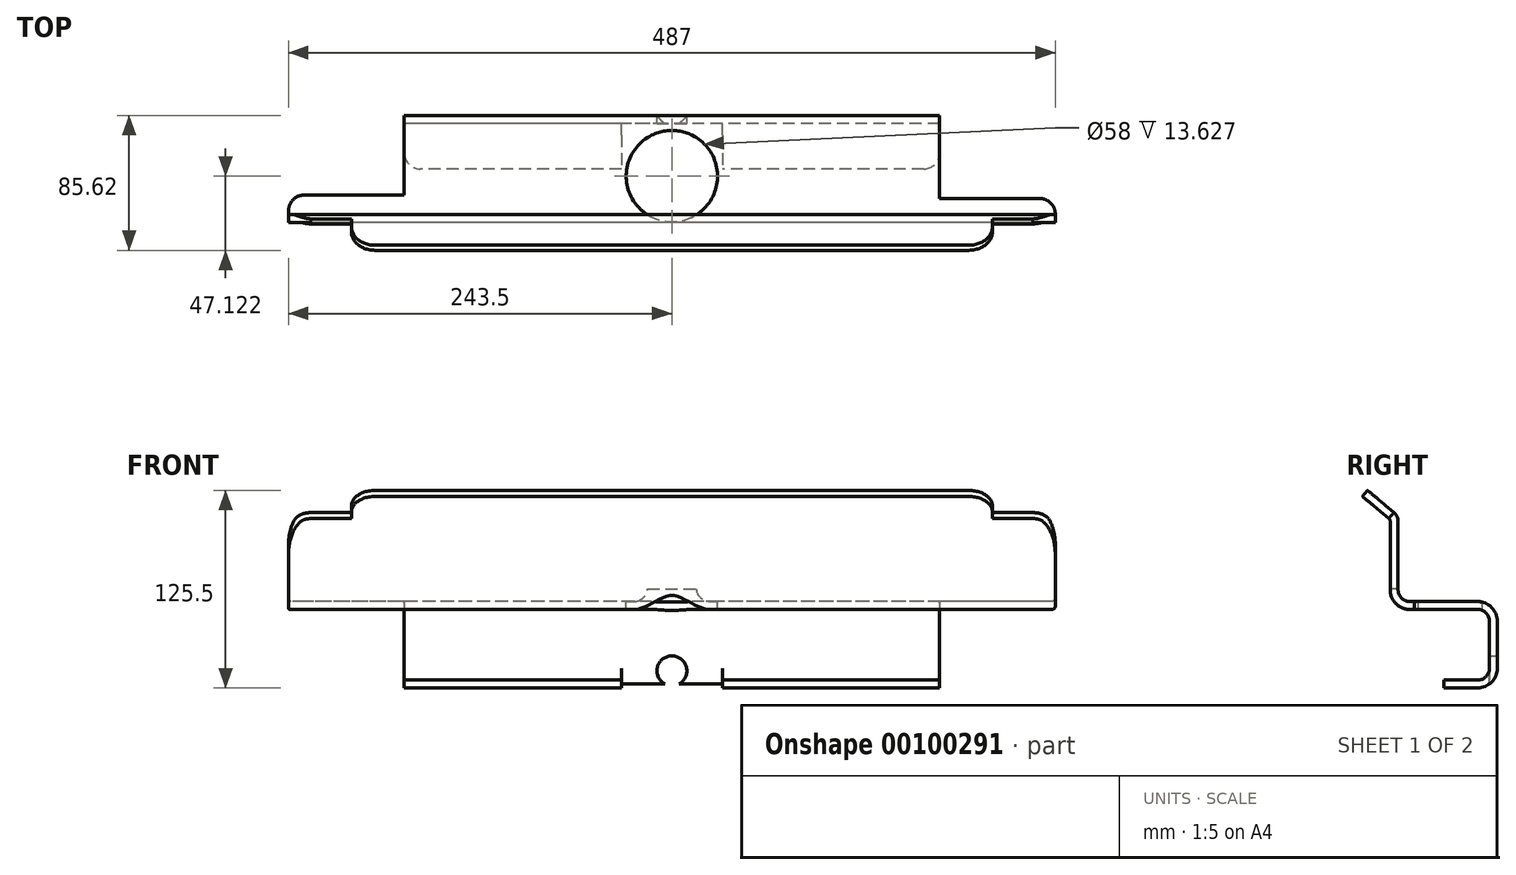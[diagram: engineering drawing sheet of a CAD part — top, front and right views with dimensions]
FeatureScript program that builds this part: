
annotation { "Feature Type Name" : "Feature", "Feature Type Description" : "" }
export const myFeature = defineFeature(function(context is Context, id is Id, definition is map)
    precondition{}
    {
        {
            var Q0;
            Q0=qCreatedBy(makeId("Right.planeOp"),FACE);
            var sketch = newSketch(context, id + "F0", { "sketchPlane" : qUnion([Q0])});
            skArc(sketch, "E0", {"start": v(-37.83, 42.97) * mm, "mid": v(-38.06, 44.03) * mm, "end": v(-38.72, 44.89) * mm});
            skLineSegment(sketch, "E1", {"start": v(-55.45, 58.92) * mm, "end": v(-52.23, 62.75) * mm});
            skArc(sketch, "E2", {"start": v(-32.83, 42.97) * mm, "mid": v(-33.53, 46.14) * mm, "end": v(-35.5, 48.72) * mm});
            skArc(sketch, "E3", {"start": v(-32.83, -0.36) * mm, "mid": v(-30.63, -5.67) * mm, "end": v(-25.33, -7.86) * mm});
            skArc(sketch, "E4", {"start": v(30.17, -20.36) * mm, "mid": v(26.51, -11.52) * mm, "end": v(17.67, -7.86) * mm});
            skLineSegment(sketch, "E5", {"start": v(-3.79, -62.75) * mm, "end": v(-3.79, -57.75) * mm});
            skArc(sketch, "E6", {"start": v(17.67, -57.75) * mm, "mid": v(22.98, -55.55) * mm, "end": v(25.17, -50.25) * mm});
            skArc(sketch, "E7", {"start": v(25.17, -20.36) * mm, "mid": v(22.98, -15.06) * mm, "end": v(17.67, -12.86) * mm});
            skArc(sketch, "E8", {"start": v(-37.83, -0.36) * mm, "mid": v(-34.17, -9.2) * mm, "end": v(-25.33, -12.86) * mm});
            skArc(sketch, "E9", {"start": v(17.67, -62.75) * mm, "mid": v(26.51, -59.09) * mm, "end": v(30.17, -50.25) * mm});
            skLineSegment(sketch, "E10", {"start": v(-35.5, 48.72) * mm, "end": v(-52.23, 62.75) * mm});
            skLineSegment(sketch, "E11", {"start": v(-38.72, 44.89) * mm, "end": v(-55.45, 58.92) * mm});
            skLineSegment(sketch, "E12", {"start": v(-32.83, 42.97) * mm, "end": v(-32.83, -0.36) * mm});
            skLineSegment(sketch, "E13", {"start": v(-37.83, 42.97) * mm, "end": v(-37.83, -0.36) * mm});
            skLineSegment(sketch, "E14", {"start": v(-25.33, -7.86) * mm, "end": v(17.67, -7.86) * mm});
            skLineSegment(sketch, "E15", {"start": v(-25.33, -12.86) * mm, "end": v(17.67, -12.86) * mm});
            skLineSegment(sketch, "E16", {"start": v(30.17, -20.36) * mm, "end": v(30.17, -50.25) * mm});
            skLineSegment(sketch, "E17", {"start": v(25.17, -20.36) * mm, "end": v(25.17, -50.25) * mm});
            skLineSegment(sketch, "E18", {"start": v(17.67, -62.75) * mm, "end": v(-3.79, -62.75) * mm});
            skLineSegment(sketch, "E19", {"start": v(17.67, -57.75) * mm, "end": v(-3.79, -57.75) * mm});
            skLineSegment(sketch, "E20", {"start": v(0, 0) * mm, "end": v(-113.48, 0) * mm, "construction": true});
            skSolve(sketch);
        }
        {
            var Q0;
            Q0=qSketchRegion(id+"F0",true);
            extrude(context, id + "F1", {"entities" : qUnion([Q0]), "endBound" : BoundingType.SYMMETRIC, "depth" : 487 * mm});
        }
        {
            var Q0;
            Q0=qCreatedBy(makeId("Top.planeOp"),FACE);
            var sketch = newSketch(context, id + "F2", { "sketchPlane" : qUnion([Q0])});
            skLineSegment(sketch, "E21.0", {"start": v(243.5, 30.17) * mm, "end": v(-243.5, 30.17) * mm, "construction": true});
            skLineSegment(sketch, "E22.0", {"start": v(243.5, 25.17) * mm, "end": v(-243.5, 25.17) * mm, "construction": true});
            skLineSegment(sketch, "E23.0", {"start": v(243.5, -3.79) * mm, "end": v(-243.5, -3.79) * mm, "construction": true});
            skLineSegment(sketch, "E24.bottom", {"start": v(-346.92, 71.4) * mm, "end": v(-170, 71.4) * mm});
            skLineSegment(sketch, "E24.top", {"start": v(-346.92, -20.36) * mm, "end": v(-170, -20.36) * mm});
            skLineSegment(sketch, "E24.left", {"start": v(-346.92, 71.4) * mm, "end": v(-346.92, -20.36) * mm});
            skLineSegment(sketch, "E24.right", {"start": v(-170, 71.4) * mm, "end": v(-170, -20.36) * mm});
            skLineSegment(sketch, "E25.bottom", {"start": v(170, 71.4) * mm, "end": v(314.46, 71.4) * mm});
            skLineSegment(sketch, "E25.top", {"start": v(170, -22.45) * mm, "end": v(314.46, -22.45) * mm});
            skLineSegment(sketch, "E25.left", {"start": v(170, 71.4) * mm, "end": v(170, -22.45) * mm});
            skLineSegment(sketch, "E25.right", {"start": v(314.46, 71.4) * mm, "end": v(314.46, -22.45) * mm});
            skLineSegment(sketch, "E26", {"start": v(-346.92, 71.4) * mm, "end": v(192.66, 71.4) * mm, "construction": true});
            skSolve(sketch);
        }
        {
            var Q0;
            Q0=makeQuery(id+"F2.imprint","IMPRINT",FACE,{"disambiguationData":[TD([[makeQuery(id+"F2.imprint","IMPRINT",EDGE,{"derivedFrom":sQuery(id+"F2.wireOp",EDGE,"E24.bottom")}),-1.0]])]});
            var Q1;
            Q1=makeQuery(id+"F2.imprint","IMPRINT",FACE,{"disambiguationData":[TD([[makeQuery(id+"F2.imprint","IMPRINT",EDGE,{"derivedFrom":sQuery(id+"F2.wireOp",EDGE,"E25.bottom")}),-1.0]])]});
            extrude(context, id + "F3", {"entities" : qUnion([Q0, Q1]), "operationType" : NewBodyOperationType.REMOVE, "endBound" : BoundingType.SYMMETRIC, "depth" : 200 * mm});
        }
        {
            var Q0;
            Q0=makeQuery(id+"F1.opExtrude","SWEPT_FACE",FACE,{"disambiguationData":[OSD([sQuery(id+"F0.wireOp",EDGE,"E10")])]});
            var sketch = newSketch(context, id + "F4", { "sketchPlane" : qUnion([Q0])});
            skLineSegment(sketch, "E27", {"start": v(247.26, -58.51) * mm, "end": v(203.5, -58.51) * mm});
            skLineSegment(sketch, "E28", {"start": v(203.5, -58.51) * mm, "end": v(203.5, -95.58) * mm});
            skLineSegment(sketch, "E29", {"start": v(203.5, -95.58) * mm, "end": v(247.26, -95.58) * mm});
            skLineSegment(sketch, "E30", {"start": v(247.26, -58.51) * mm, "end": v(247.26, -95.58) * mm});
            skLineSegment(sketch, "E31", {"start": v(247.26, -95.58) * mm, "end": v(-263.65, -95.58) * mm, "construction": true});
            skLineSegment(sketch, "E32", {"start": v(247.26, -58.51) * mm, "end": v(-263.65, -58.51) * mm, "construction": true});
            skLineSegment(sketch, "E33.bottom", {"start": v(-203.5, -95.58) * mm, "end": v(-252.3, -95.58) * mm});
            skLineSegment(sketch, "E33.top", {"start": v(-203.5, -58.51) * mm, "end": v(-252.3, -58.51) * mm});
            skLineSegment(sketch, "E33.left", {"start": v(-203.5, -95.58) * mm, "end": v(-203.5, -58.51) * mm});
            skLineSegment(sketch, "E33.right", {"start": v(-252.3, -95.58) * mm, "end": v(-252.3, -58.51) * mm});
            skSolve(sketch);
        }
        {
            var Q0;
            {var subQ1=sQuery(id+"F0.wireOp",EDGE,"E10");var subQ2=makeQuery(id+"F1.opExtrude","CAP_EDGE",EDGE,{"disambiguationData":[OSD([subQ1])],"isStart":false});Q0=makeQuery(id+"F4.imprint","IMPRINT",FACE,{"disambiguationData":[TD([[makeQuery(id+"F4.imprint","IMPRINT",EDGE,{"derivedFrom":subQ2}),-1.0]])]});}
            var Q1;
            {var subQ6=sQuery(id+"F4.wireOp",EDGE,"E29");Q1=makeQuery(id+"F4.imprint","IMPRINT",FACE,{"disambiguationData":[TD([[makeQuery(id+"F4.imprint","IMPRINT",EDGE,{"derivedFrom":subQ6}),1.0]])]});}
            var Q2;
            {var subQ2=sQuery(id+"F4.wireOp",EDGE,"E33.bottom");Q2=makeQuery(id+"F4.imprint","IMPRINT",FACE,{"disambiguationData":[TD([[makeQuery(id+"F4.imprint","IMPRINT",EDGE,{"derivedFrom":subQ2}),-1.0]])]});}
            var Q3;
            {var subQ1=sQuery(id+"F0.wireOp",EDGE,"E10");var subQ2=makeQuery(id+"F1.opExtrude","CAP_EDGE",EDGE,{"disambiguationData":[OSD([subQ1])],"isStart":true});Q3=makeQuery(id+"F4.imprint","IMPRINT",FACE,{"disambiguationData":[TD([[makeQuery(id+"F4.imprint","IMPRINT",EDGE,{"derivedFrom":subQ2}),1.0]])]});}
            extrude(context, id + "F5", {"entities" : qUnion([Q0, Q1, Q2, Q3]), "operationType" : NewBodyOperationType.REMOVE, "endBound" : BoundingType.SYMMETRIC, "oppositeDirection" : true, "depth" : 25 * mm});
        }
        {
            var Q0;
            Q0=makeQuery(id+"F5.boolean.opBoolean","INTERSECT",EDGE,{"derivedFrom":[makeQuery(id+"F1.opExtrude","SWEPT_FACE",FACE,{"disambiguationData":[OSD([sQuery(id+"F0.wireOp",EDGE,"E1")])]}),makeQuery(id+"F5.opExtrude","SWEPT_FACE",FACE,{"disambiguationData":[OSD([sQuery(id+"F4.wireOp",EDGE,"E28")])]})]});
            var Q1;
            Q1=makeQuery(id+"F5.boolean.opBoolean","INTERSECT",EDGE,{"derivedFrom":[makeQuery(id+"F1.opExtrude","SWEPT_FACE",FACE,{"disambiguationData":[OSD([sQuery(id+"F0.wireOp",EDGE,"E1")])]}),makeQuery(id+"F5.opExtrude","SWEPT_FACE",FACE,{"disambiguationData":[OSD([sQuery(id+"F4.wireOp",EDGE,"E33.left")])]})]});
            var Q2;
            Q2=makeQuery(id+"F5.boolean.opBoolean","INTERSECT",EDGE,{"derivedFrom":[makeQuery(id+"F1.opExtrude","CAP_FACE",FACE,{"disambiguationData":[OSD([sQuery(id+"F0.wireOp",EDGE,"E0"),sQuery(id+"F0.wireOp",EDGE,"E1"),sQuery(id+"F0.wireOp",EDGE,"E2"),sQuery(id+"F0.wireOp",EDGE,"E3"),sQuery(id+"F0.wireOp",EDGE,"E4"),sQuery(id+"F0.wireOp",EDGE,"E5"),sQuery(id+"F0.wireOp",EDGE,"E6"),sQuery(id+"F0.wireOp",EDGE,"E7"),sQuery(id+"F0.wireOp",EDGE,"E8"),sQuery(id+"F0.wireOp",EDGE,"E9"),sQuery(id+"F0.wireOp",EDGE,"E10"),sQuery(id+"F0.wireOp",EDGE,"E11"),sQuery(id+"F0.wireOp",EDGE,"E12"),sQuery(id+"F0.wireOp",EDGE,"E13"),sQuery(id+"F0.wireOp",EDGE,"E14"),sQuery(id+"F0.wireOp",EDGE,"E15"),sQuery(id+"F0.wireOp",EDGE,"E16"),sQuery(id+"F0.wireOp",EDGE,"E17"),sQuery(id+"F0.wireOp",EDGE,"E18"),sQuery(id+"F0.wireOp",EDGE,"E19")])],"isStart":true}),makeQuery(id+"F5.opExtrude","SWEPT_FACE",FACE,{"disambiguationData":[OSD([sQuery(id+"F4.wireOp",EDGE,"E33.top")])]})]});
            var Q3;
            Q3=makeQuery(id+"F5.boolean.opBoolean","INTERSECT",EDGE,{"derivedFrom":[makeQuery(id+"F1.opExtrude","CAP_FACE",FACE,{"disambiguationData":[OSD([sQuery(id+"F0.wireOp",EDGE,"E0"),sQuery(id+"F0.wireOp",EDGE,"E1"),sQuery(id+"F0.wireOp",EDGE,"E2"),sQuery(id+"F0.wireOp",EDGE,"E3"),sQuery(id+"F0.wireOp",EDGE,"E4"),sQuery(id+"F0.wireOp",EDGE,"E5"),sQuery(id+"F0.wireOp",EDGE,"E6"),sQuery(id+"F0.wireOp",EDGE,"E7"),sQuery(id+"F0.wireOp",EDGE,"E8"),sQuery(id+"F0.wireOp",EDGE,"E9"),sQuery(id+"F0.wireOp",EDGE,"E10"),sQuery(id+"F0.wireOp",EDGE,"E11"),sQuery(id+"F0.wireOp",EDGE,"E12"),sQuery(id+"F0.wireOp",EDGE,"E13"),sQuery(id+"F0.wireOp",EDGE,"E14"),sQuery(id+"F0.wireOp",EDGE,"E15"),sQuery(id+"F0.wireOp",EDGE,"E16"),sQuery(id+"F0.wireOp",EDGE,"E17"),sQuery(id+"F0.wireOp",EDGE,"E18"),sQuery(id+"F0.wireOp",EDGE,"E19")])],"isStart":false}),makeQuery(id+"F5.opExtrude","SWEPT_FACE",FACE,{"disambiguationData":[OSD([sQuery(id+"F4.wireOp",EDGE,"E27")])]})]});
            fillet(context, id + "F6", {"entities" : qUnion([Q0, Q1, Q2, Q3]), "radius" : 15 * mm, "tangentPropagation" : true, "allowEdgeOverflow" : false});
        }
        {
            var Q0;
            Q0=makeQuery(id+"F1.opExtrude","SWEPT_FACE",FACE,{"disambiguationData":[OSD([sQuery(id+"F0.wireOp",EDGE,"E18")])]});
            var sketch = newSketch(context, id + "F7", { "sketchPlane" : qUnion([Q0])});
            skLineSegment(sketch, "E34.bottom", {"start": v(32, -25.17) * mm, "end": v(-32, -25.17) * mm});
            skLineSegment(sketch, "E34.top", {"start": v(32, 15.24) * mm, "end": v(-32, 15.24) * mm});
            skLineSegment(sketch, "E34.left", {"start": v(32, -25.17) * mm, "end": v(32, 15.24) * mm});
            skLineSegment(sketch, "E34.right", {"start": v(-32, -25.17) * mm, "end": v(-32, 15.24) * mm});
            skSolve(sketch);
        }
        {
            var Q0;
            {var subQ0=sQuery(id+"F7.wireOp",EDGE,"E34.bottom");Q0=makeQuery(id+"F7.imprint","IMPRINT",FACE,{"disambiguationData":[TD([[makeQuery(id+"F7.imprint","IMPRINT",EDGE,{"derivedFrom":subQ0}),-1.0]])]});}
            var Q1;
            {var subQ0=sQuery(id+"F7.wireOp",EDGE,"E34.top");Q1=makeQuery(id+"F7.imprint","IMPRINT",FACE,{"disambiguationData":[TD([[makeQuery(id+"F7.imprint","IMPRINT",EDGE,{"derivedFrom":subQ0}),1.0]])]});}
            var Q2;
            {var subQ0=sQuery(id+"F7.wireOp",EDGE,"E34.left");var subQ1=sQuery(id+"F0.wireOp",EDGE,"E18");var subQ2=makeQuery(id+"F1.opExtrude","SWEPT_EDGE",EDGE,{"disambiguationData":[OSD([sQuery(id+"F0.wireOp",EDGE,"E9"),subQ1])]});var subQ3=makeQuery(id+"F7.imprint","INTERSECT",VERTEX,{"derivedFrom":[subQ2,subQ0]});Q2=makeQuery(id+"F7.imprint","IMPRINT",FACE,{"disambiguationData":[TD([[makeQuery(id+"F7.imprint","IMPRINT",EDGE,{"disambiguationData":[TD([[subQ3,-1.0]])],"derivedFrom":subQ0}),1.0]])]});}
            extrude(context, id + "F8", {"entities" : qUnion([Q0, Q1, Q2]), "operationType" : NewBodyOperationType.REMOVE, "oppositeDirection" : true, "depth" : 25 * mm});
        }
        {
            var Q0;
            Q0=makeQuery(id+"F1.opExtrude","SWEPT_FACE",FACE,{"disambiguationData":[OSD([sQuery(id+"F0.wireOp",EDGE,"E14")])]});
            var sketch = newSketch(context, id + "F9", { "sketchPlane" : qUnion([Q0])});
            skCircle(sketch, "E35", {"center": v(0, -8.33) * mm, "radius": 29 * mm});
            skSolve(sketch);
        }
        {
            var Q0;
            Q0=qSketchRegion(id+"F9",true);
            extrude(context, id + "F10", {"entities" : qUnion([Q0]), "operationType" : NewBodyOperationType.REMOVE, "oppositeDirection" : true, "depth" : 6 * mm, "hasSecondDirection" : true, "secondDirectionOppositeDirection" : false, "secondDirectionDepth" : 8 * mm});
        }
        {
            var Q0;
            Q0=makeQuery(id+"F1.opExtrude","SWEPT_FACE",FACE,{"disambiguationData":[OSD([sQuery(id+"F0.wireOp",EDGE,"E16")])]});
            var sketch = newSketch(context, id + "F11", { "sketchPlane" : qUnion([Q0])});
            skCircle(sketch, "E36", {"center": v(0, -51.86) * mm, "radius": 9.5 * mm});
            skPoint(sketch, "E37", {"position": v(0, -20.36) * mm});
            skSolve(sketch);
        }
        {
            var Q0;
            Q0=qSketchRegion(id+"F11",true);
            extrude(context, id + "F12", {"entities" : qUnion([Q0]), "operationType" : NewBodyOperationType.REMOVE, "oppositeDirection" : true, "depth" : 25 * mm});
        }
        {
            var Q0;
            Q0=makeQuery(id+"F3.boolean.opBoolean","INTERSECT",EDGE,{"derivedFrom":[makeQuery(id+"F1.opExtrude","CAP_FACE",FACE,{"disambiguationData":[OSD([sQuery(id+"F0.wireOp",EDGE,"E0"),sQuery(id+"F0.wireOp",EDGE,"E1"),sQuery(id+"F0.wireOp",EDGE,"E2"),sQuery(id+"F0.wireOp",EDGE,"E3"),sQuery(id+"F0.wireOp",EDGE,"E4"),sQuery(id+"F0.wireOp",EDGE,"E5"),sQuery(id+"F0.wireOp",EDGE,"E6"),sQuery(id+"F0.wireOp",EDGE,"E7"),sQuery(id+"F0.wireOp",EDGE,"E8"),sQuery(id+"F0.wireOp",EDGE,"E9"),sQuery(id+"F0.wireOp",EDGE,"E10"),sQuery(id+"F0.wireOp",EDGE,"E11"),sQuery(id+"F0.wireOp",EDGE,"E12"),sQuery(id+"F0.wireOp",EDGE,"E13"),sQuery(id+"F0.wireOp",EDGE,"E14"),sQuery(id+"F0.wireOp",EDGE,"E15"),sQuery(id+"F0.wireOp",EDGE,"E16"),sQuery(id+"F0.wireOp",EDGE,"E17"),sQuery(id+"F0.wireOp",EDGE,"E18"),sQuery(id+"F0.wireOp",EDGE,"E19")])],"isStart":false}),makeQuery(id+"F3.opExtrude","SWEPT_FACE",FACE,{"disambiguationData":[OSD([sQuery(id+"F2.wireOp",EDGE,"E25.top")])]})]});
            var Q1;
            Q1=makeQuery(id+"F3.boolean.opBoolean","INTERSECT",EDGE,{"derivedFrom":[makeQuery(id+"F1.opExtrude","CAP_FACE",FACE,{"disambiguationData":[OSD([sQuery(id+"F0.wireOp",EDGE,"E0"),sQuery(id+"F0.wireOp",EDGE,"E1"),sQuery(id+"F0.wireOp",EDGE,"E2"),sQuery(id+"F0.wireOp",EDGE,"E3"),sQuery(id+"F0.wireOp",EDGE,"E4"),sQuery(id+"F0.wireOp",EDGE,"E5"),sQuery(id+"F0.wireOp",EDGE,"E6"),sQuery(id+"F0.wireOp",EDGE,"E7"),sQuery(id+"F0.wireOp",EDGE,"E8"),sQuery(id+"F0.wireOp",EDGE,"E9"),sQuery(id+"F0.wireOp",EDGE,"E10"),sQuery(id+"F0.wireOp",EDGE,"E11"),sQuery(id+"F0.wireOp",EDGE,"E12"),sQuery(id+"F0.wireOp",EDGE,"E13"),sQuery(id+"F0.wireOp",EDGE,"E14"),sQuery(id+"F0.wireOp",EDGE,"E15"),sQuery(id+"F0.wireOp",EDGE,"E16"),sQuery(id+"F0.wireOp",EDGE,"E17"),sQuery(id+"F0.wireOp",EDGE,"E18"),sQuery(id+"F0.wireOp",EDGE,"E19")])],"isStart":true}),makeQuery(id+"F3.opExtrude","SWEPT_FACE",FACE,{"disambiguationData":[OSD([sQuery(id+"F2.wireOp",EDGE,"E24.top")])]})]});
            var Q2;
            Q2=makeQuery(id+"F3.boolean.opBoolean","INTERSECT",EDGE,{"derivedFrom":[makeQuery(id+"F1.opExtrude","SWEPT_FACE",FACE,{"disambiguationData":[OSD([sQuery(id+"F0.wireOp",EDGE,"E5")])]}),makeQuery(id+"F3.opExtrude","SWEPT_FACE",FACE,{"disambiguationData":[OSD([sQuery(id+"F2.wireOp",EDGE,"E25.left")])]})]});
            var Q3;
            Q3=makeQuery(id+"F3.boolean.opBoolean","INTERSECT",EDGE,{"derivedFrom":[makeQuery(id+"F1.opExtrude","SWEPT_FACE",FACE,{"disambiguationData":[OSD([sQuery(id+"F0.wireOp",EDGE,"E5")])]}),makeQuery(id+"F3.opExtrude","SWEPT_FACE",FACE,{"disambiguationData":[OSD([sQuery(id+"F2.wireOp",EDGE,"E24.right")])]})]});
            fillet(context, id + "F13", {"entities" : qUnion([Q0, Q1, Q2, Q3]), "radius" : 10 * mm, "tangentPropagation" : true, "allowEdgeOverflow" : false});
        }
    });
